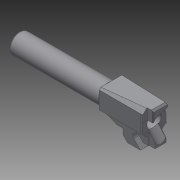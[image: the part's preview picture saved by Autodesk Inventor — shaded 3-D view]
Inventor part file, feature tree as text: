
AUTODESK INVENTOR PART (.ipt)
format: ipt  version: 2014 SP2 (Build 180246200, 246)  size: 8,766,464 bytes
history: native  units: in
note: dims shown in document units (in); Inventor stores cm internally (conversion verified against a paired STEP export)
features: sketch x25, projected_geometry x15, extrude x12, other x4, plane x4, mirror x3, revolve x3, fillet x3, sweep x2, loft x1, pattern_circular x1, chamfer x1, emboss x1, reference x1
ambient origin geometry x8: Origin, YZ Plane, XZ Plane, XY Plane, X Axis, Y Axis, Z Axis, Center Point
bodies: Solid1 (feature_tree)
feature tree (76):
  other  "Barrel"
  extrude  "Extrusion1"  Depth=0.7455in
  extrude  "Extrusion2"  Depth=0.2825in
  extrude  "Extrusion3"  Depth=0.2165in
  plane  "Work Plane1"
  extrude  "Extrusion4"  Depth=0.1605in
  mirror  "Mirror1"
  sketch  "Sketch5"  dims[d23=0.2475in d24=45.0deg]
  sketch  "Sketch6"  dims[d27=0.639in d29=45.0deg]
  loft  "Loft1"
  extrude  "Extrusion5"  TaperAngle=45.0deg  [1 undecoded]
  extrude  "Extrusion6"  Depth=0.2965in
  other  "Work Axis1"
  sketch  "Sketch10"  dims[d42=0.3345in d44=45.0deg]
  revolve  "Revolution1"  [1 undecoded]
  extrude  "Extrusion7"  Depth=0.6565in TaperAngle=0.0deg
  extrude  "Extrusion8"  TaperAngle=45.0deg  [1 undecoded]
  sketch  "Sketch13"  dims[d52=0.4045in d53=0.6565in d54=0.0in d55=-0.016in]
  extrude  "Extrusion9"  TaperAngle=45.0deg  [1 undecoded]
  revolve  "Revolution2"  [1 undecoded]
  plane  "Work Plane3"
  extrude  "Extrusion10"  Depth=0.6565in TaperAngle=0.0deg
  fillet  "Fillet1"  [1 undecoded]
  sweep  "Sweep1"
  mirror  "Mirror2"
  fillet  "Fillet2"  Radius=0.7559in
  sketch  "Sketch17"  dims[d65=0.0in d66=90.0deg]
  sketch  "Sketch18"  dims[d67=0.5505in]
  sweep  "Sweep2"
  pattern_circular  "Circular Pattern1"  [2 undecoded]
  revolve  "Revolution3"  Angle=90.0deg
  fillet  "Fillet3"  Radius=2.512in
  sketch  "Sketch20"  dims[d70=0.3472in]
  extrude  "Extrusion11"  Depth=0.005in TaperAngle=0.0deg
  chamfer  "Chamfer1"  Distance=0.0135in
  plane  "Work Plane4"
  extrude  "Extrusion12"  TaperAngle=90.0deg  [1 undecoded]
  mirror  "Mirror3"
  emboss  "Emboss1"
  sketch  "Sketch1"  dims[d1=4.0617in d5=0.7455in]
  other  "Image1"
  sketch  "Sketch2"  dims[d6=1.35in d15=0.2825in]
  projected_geometry  "Projected Loop1"
  sketch  "Sketch3"  dims[d17=0.207in d18=0.2165in]
  sketch  "Sketch4"  dims[d19=0.86in d21=0.1605in]
  projected_geometry  "Projected Loop2"
  sketch  "Sketch7"  dims[d30=0.064in d31=0.2965in]
  sketch  "Sketch8"  dims[d33=0.3595in d34=0.18in]
  reference  "Reference1"
  sketch  "Sketch9"  dims[d38=0.9225in d39=0.6565in d40=0.0in]
  projected_geometry  "Projected Loop3"
  sketch  "Sketch11"  dims[d45=0.514in d47=45.0deg]
  projected_geometry  "Projected Loop4"
  sketch  "Sketch12"  dims[d49=0.6565in d50=0.0in d51=0.0645in]
  projected_geometry  "Projected Loop5"
  sketch  "Sketch14"  dims[d56=0.2035in d57=0.0in d59=0.114in d60=0.7559in]
  plane  "Work Plane2"
  sketch  "Sketch15"  dims[d61=0.6528in d62=0.7559in]
  projected_geometry  "Projected Loop6"
  sketch  "Sketch16"  dims[d63=0.0in d64=90.0deg]
  projected_geometry  "Projected Loop7"
  sketch  "3D Sketch1"
  sketch  "3D Sketch2"
  other  "Helical Curve1"
  sketch  "Sketch19"  dims[d68=2.512in d69=0.0in]
  sketch  "Sketch21"  dims[d71=2.512in d72=0.0in]
  sketch  "Sketch22"  dims[d73=0.606in]
  sketch  "Sketch23"  dims[d74=0.3855in d75=0.3925in d76=90.0deg d77=2.512in d78=0.0in d79=0.0135in d80=0.0in d81=0.0135in d82=0.0in d83=90.0deg d84=0.3436in d85=0.451in d86=0.0in d87=0.962in d88=0.01in d89=0.0in d90=0.025in d91=0.3551in d92=0.098in d93=2.3622in d95=360.0deg d97=9.8425in d98=3.096in d99=0.347in d100=0.0in d101=0.0in d102=2.3622in d103=360.0deg d105=90.0deg d106=0.05in d107=0.0in d108=0.0in d109=0.025in d110=0.125in d111=45.0deg d112=0.125in d113=0.6528in d114=0.9022in d115=0.0in d116=0.005in d117=0.0in]
  projected_geometry  "Project Cut Edges1"
  projected_geometry  "Project Cut Edges2"
  projected_geometry  "Project Cut Edges3"
  projected_geometry  "Project Cut Edges4"
  projected_geometry  "Project Cut Edges5"
  projected_geometry  "Project Cut Edges6"
  projected_geometry  "Project Cut Edges7"
  projected_geometry  "Project Cut Edges8"
note: 9 required parameter values undecoded (feature->parameter linkage not recoverable at this tier; creation-order binding heuristic only, values carry confidence <= 0.55)